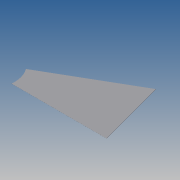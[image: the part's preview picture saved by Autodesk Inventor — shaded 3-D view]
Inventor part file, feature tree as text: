
AUTODESK INVENTOR PART (.ipt)
format: ipt  version: 2014 SP1 (Build 180222100, 222)  size: 74,752 bytes
history: native  units: in
note: dims shown in document units (in); Inventor stores cm internally (conversion verified against a paired STEP export)
features: extrude x1, sketch x1
ambient origin geometry x8: Origin, YZ Plane, XZ Plane, XY Plane, X Axis, Y Axis, Z Axis, Center Point
bodies: Solid1 (feature_tree)
feature tree (2):
  extrude  "Extrusion1"  TaperAngle=150.0deg  [1 undecoded]
  sketch  "Sketch1"  dims[d1=118.1102in d2=150.0deg d3=39.3701in d11=1.9685in d12=65.3543in d13=48.0315in d14=75.0deg d16=30.0deg d17=0.0394in d18=0.0in]
note: 1 required parameter value undecoded (feature->parameter linkage not recoverable at this tier; creation-order binding heuristic only, values carry confidence <= 0.55)
